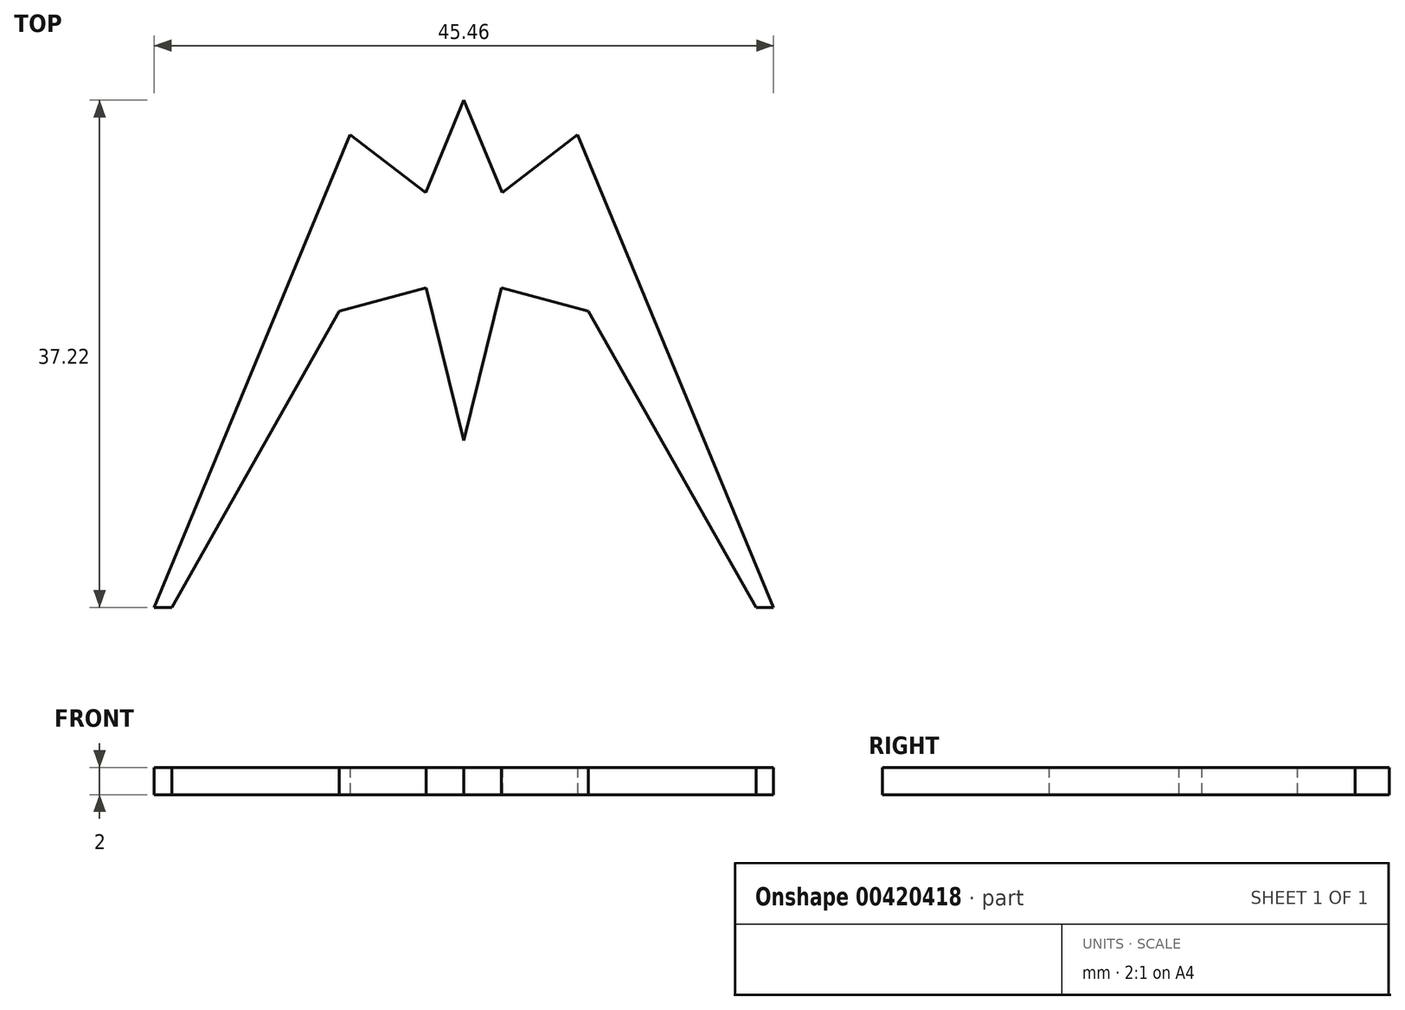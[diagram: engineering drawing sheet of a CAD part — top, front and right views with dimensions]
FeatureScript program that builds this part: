
annotation { "Feature Type Name" : "Feature", "Feature Type Description" : "" }
export const myFeature = defineFeature(function(context is Context, id is Id, definition is map)
    precondition{}
    {
        {
            var Q0;
            Q0=qCreatedBy(makeId("Top.planeOp"),FACE);
            var sketch = newSketch(context, id + "F0", { "sketchPlane" : qUnion([Q0])});
            skLineSegment(sketch, "E0", {"start": v(0, 14.35) * mm, "end": v(2.87, 7.42) * mm});
            skLineSegment(sketch, "E1", {"start": v(2.87, 7.42) * mm, "end": v(8.42, 11.68) * mm});
            skLineSegment(sketch, "E2", {"start": v(8.42, 11.68) * mm, "end": v(22.96, -23.41) * mm});
            skLineSegment(sketch, "E3", {"start": v(22.96, -23.41) * mm, "end": v(21.36, -23.41) * mm});
            skLineSegment(sketch, "E4", {"start": v(21.36, -23.41) * mm, "end": v(9.05, -1.65) * mm});
            skLineSegment(sketch, "E5", {"start": v(9.05, -1.65) * mm, "end": v(2.87, 0) * mm});
            skLineSegment(sketch, "E6", {"start": v(2.87, 0) * mm, "end": v(0, -11.65) * mm});
            skLineSegment(sketch, "E7", {"start": v(0, 14.35) * mm, "end": v(0, -11.65) * mm, "construction": true});
            skLineSegment(sketch, "E8.MirrorCS", {"start": v(0, 14.35) * mm, "end": v(-2.87, 7.42) * mm});
            skLineSegment(sketch, "E9.MirrorCS", {"start": v(-2.87, 7.42) * mm, "end": v(-8.42, 11.68) * mm});
            skLineSegment(sketch, "E10.MirrorCS", {"start": v(-8.42, 11.68) * mm, "end": v(-22.96, -23.41) * mm});
            skLineSegment(sketch, "E11.MirrorCS", {"start": v(-2.87, 0) * mm, "end": v(0, -11.65) * mm});
            skLineSegment(sketch, "E12.MirrorCS", {"start": v(-9.05, -1.65) * mm, "end": v(-2.87, 0) * mm});
            skLineSegment(sketch, "E13.MirrorCS", {"start": v(-21.36, -23.41) * mm, "end": v(-9.05, -1.65) * mm});
            skLineSegment(sketch, "E14.MirrorCS", {"start": v(-22.96, -23.41) * mm, "end": v(-21.36, -23.41) * mm});
            skLineSegment(sketch, "E15.0", {"start": v(0, 13.96) * mm, "end": v(-2.8, 7.18) * mm});
            skLineSegment(sketch, "E15.1", {"start": v(-2.8, 7.18) * mm, "end": v(-8.36, 11.44) * mm});
            skLineSegment(sketch, "E15.2", {"start": v(-8.36, 11.44) * mm, "end": v(-22.73, -23.26) * mm});
            skLineSegment(sketch, "E15.3", {"start": v(21.45, -23.26) * mm, "end": v(9.15, -1.52) * mm});
            skLineSegment(sketch, "E15.4", {"start": v(22.73, -23.26) * mm, "end": v(21.45, -23.26) * mm});
            skLineSegment(sketch, "E15.5", {"start": v(8.36, 11.44) * mm, "end": v(22.73, -23.26) * mm});
            skLineSegment(sketch, "E15.6", {"start": v(2.8, 7.18) * mm, "end": v(8.36, 11.44) * mm});
            skLineSegment(sketch, "E15.7", {"start": v(9.15, -1.52) * mm, "end": v(2.76, 0.18) * mm});
            skLineSegment(sketch, "E15.8", {"start": v(2.76, 0.18) * mm, "end": v(0, -11.02) * mm});
            skLineSegment(sketch, "E15.9", {"start": v(-2.76, 0.18) * mm, "end": v(0, -11.02) * mm});
            skLineSegment(sketch, "E15.10", {"start": v(0, 13.96) * mm, "end": v(2.8, 7.18) * mm});
            skLineSegment(sketch, "E15.11", {"start": v(-9.15, -1.52) * mm, "end": v(-2.76, 0.18) * mm});
            skLineSegment(sketch, "E15.12", {"start": v(-21.45, -23.26) * mm, "end": v(-9.15, -1.52) * mm});
            skLineSegment(sketch, "E15.13", {"start": v(-22.73, -23.26) * mm, "end": v(-21.45, -23.26) * mm});
            skSolve(sketch);
        }
        {
            var Q0;
            Q0=makeQuery(id+"F0.imprint","IMPRINT",FACE,{"disambiguationData":[TD([[makeQuery(id+"F0.imprint","IMPRINT",EDGE,{"derivedFrom":sQuery(id+"F0.wireOp",EDGE,"E15.0")}),1.0]])]});
            extrude(context, id + "F1", {"entities" : qUnion([Q0]), "depth" : 2 * mm});
        }
    });
